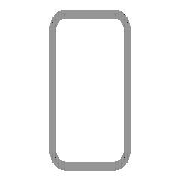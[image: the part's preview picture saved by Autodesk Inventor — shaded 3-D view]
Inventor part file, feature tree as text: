
AUTODESK INVENTOR PART (.ipt)
format: ipt  version: 2025 (Build 290162010, 162A)  size: 129,536 bytes
history: native  units: mm (DEFAULTED — no unit token found)
features: other x3, sketch x1, plane x1
ambient origin geometry x8: Origin, YZ Plane, XZ Plane, XY Plane, X Axis, Y Axis, Z Axis, Center Point
bodies: Solid1 (feature_tree), Body (feature_tree)
feature tree (5):
  other  "Driven Length"
  other  "Start plane"
  other  "End plane"
  sketch  "Sketch3"  dims[d3=1700.0mm d4=0.0mm d7=4.0mm d9=20.0mm d11=40.0mm d12=2.0mm d13=-0.0mm d14=1700.0mm d15=10.0mm d16=20.0mm d17=90.0deg d18=1700.0mm]
  plane  "Work Plane3"
